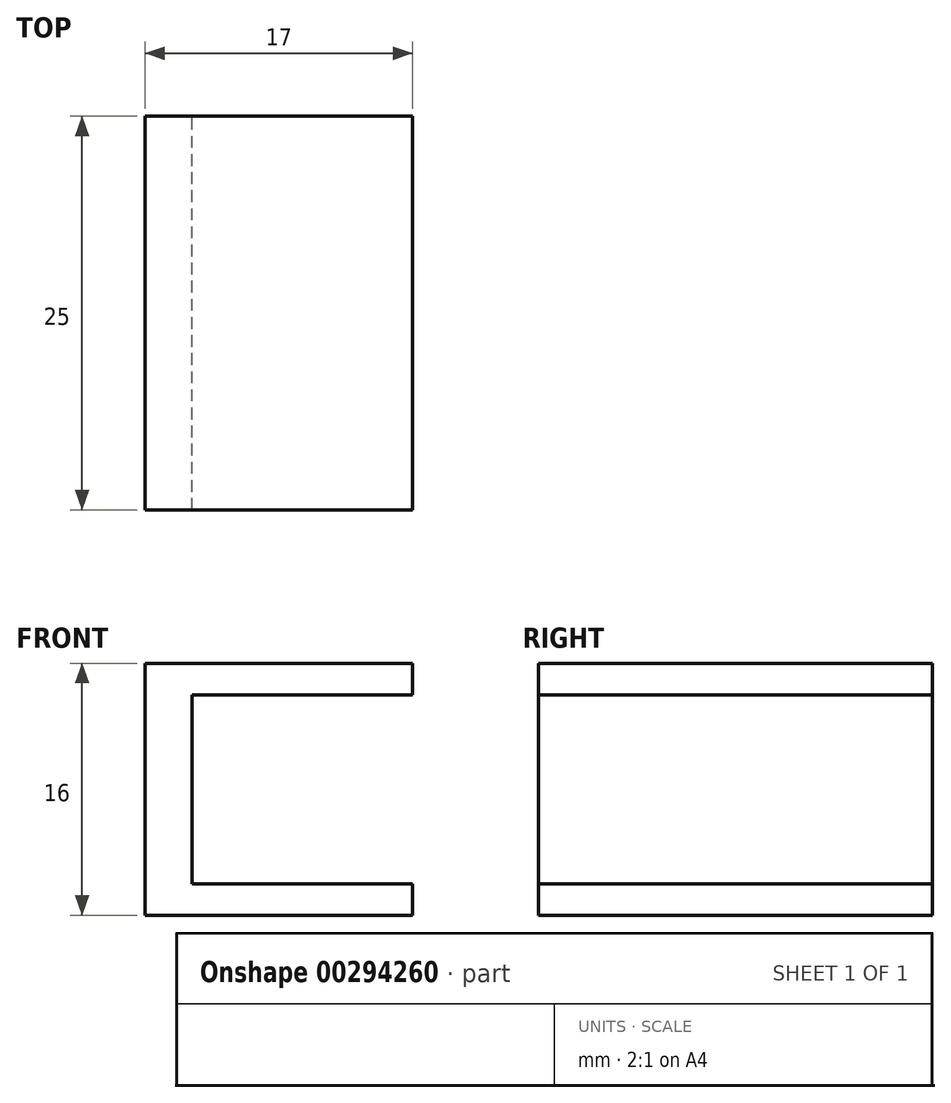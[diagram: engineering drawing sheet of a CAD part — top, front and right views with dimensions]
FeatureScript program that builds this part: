
annotation { "Feature Type Name" : "Feature", "Feature Type Description" : "" }
export const myFeature = defineFeature(function(context is Context, id is Id, definition is map)
    precondition{}
    {
        {
            var Q0;
            Q0=qCreatedBy(makeId("Front.planeOp"),FACE);
            var sketch = newSketch(context, id + "F0", { "sketchPlane" : qUnion([Q0])});
            skLineSegment(sketch, "E0.bottom", {"start": v(0, 0) * mm, "end": v(-17, 0) * mm});
            skLineSegment(sketch, "E0.top", {"start": v(0, 16) * mm, "end": v(-17, 16) * mm});
            skLineSegment(sketch, "E0.left", {"start": v(0, 0) * mm, "end": v(0, 2) * mm});
            skLineSegment(sketch, "E0.right", {"start": v(-17, 0) * mm, "end": v(-17, 16) * mm});
            skLineSegment(sketch, "E1", {"start": v(0, 14) * mm, "end": v(-14, 14) * mm});
            skLineSegment(sketch, "E2", {"start": v(-14, 14) * mm, "end": v(-14, 2) * mm});
            skLineSegment(sketch, "E3", {"start": v(-14, 2) * mm, "end": v(0, 2) * mm});
            skLineSegment(sketch, "E4.trimOffspring", {"start": v(0, 14) * mm, "end": v(0, 16) * mm});
            skSolve(sketch);
        }
        {
            var Q0;
            Q0 = qSketchRegion(id + "F0", true);
            extrude(context, id + "F1", {"entities" : qUnion([Q0]), "depth" : 25 * mm});
        }
    });
